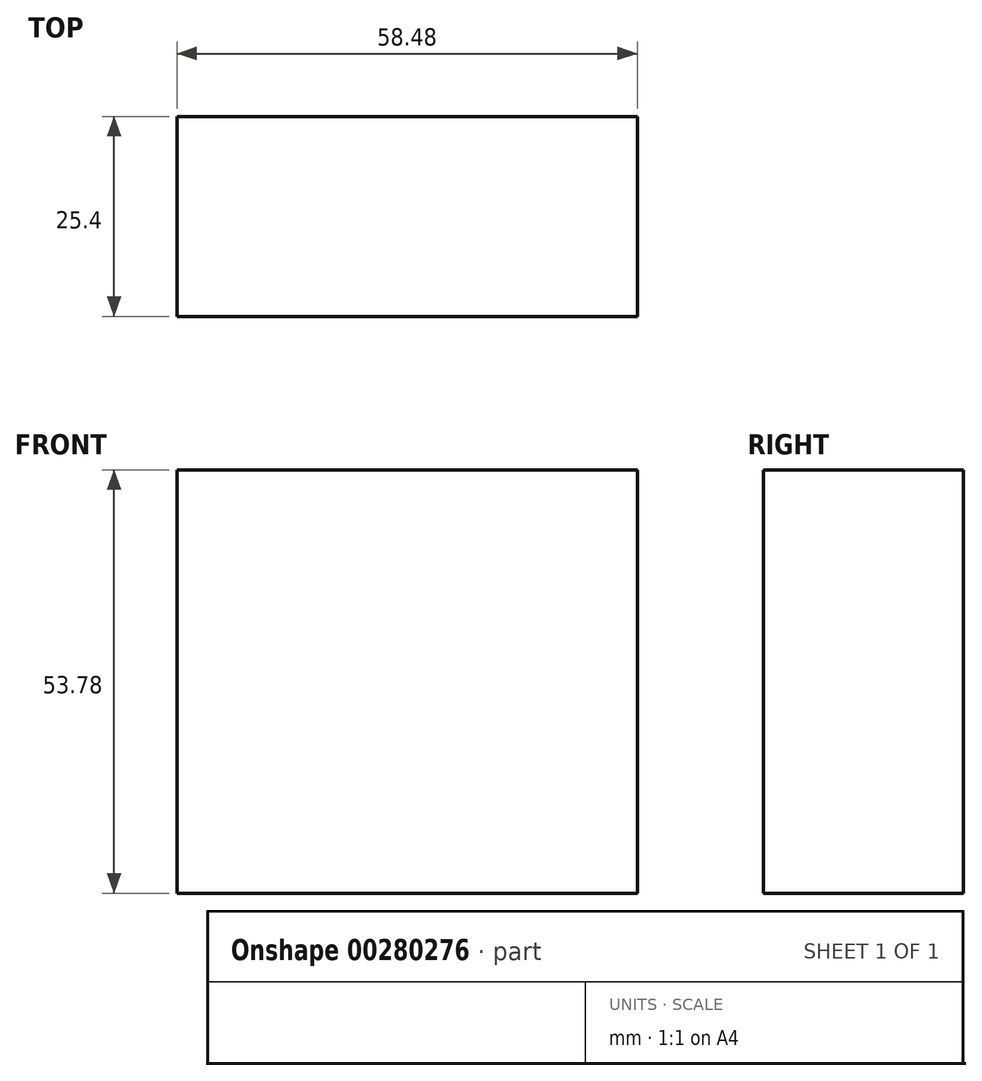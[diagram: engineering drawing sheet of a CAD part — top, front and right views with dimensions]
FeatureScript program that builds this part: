
annotation { "Feature Type Name" : "Feature", "Feature Type Description" : "" }
export const myFeature = defineFeature(function(context is Context, id is Id, definition is map)
    precondition{}
    {
        {
            var Q0;
            Q0=qCreatedBy(makeId("Front.planeOp"),FACE);
            var sketch = newSketch(context, id + "F0", { "sketchPlane" : qUnion([Q0])});
            skLineSegment(sketch, "E0.bottom", {"start": v(9.27, 28.85) * mm, "end": v(-49.2, 28.85) * mm});
            skLineSegment(sketch, "E0.top", {"start": v(9.27, -24.93) * mm, "end": v(-49.2, -24.93) * mm});
            skLineSegment(sketch, "E0.left", {"start": v(9.27, 28.85) * mm, "end": v(9.27, -24.93) * mm});
            skLineSegment(sketch, "E0.right", {"start": v(-49.2, 28.85) * mm, "end": v(-49.2, -24.93) * mm});
            skSolve(sketch);
        }
        {
            var Q0;
            Q0 = qSketchRegion(id + "F0", true);
            extrude(context, id + "F1", {"entities" : qUnion([Q0]), "depth" : 25.4 * mm});
        }
    });
